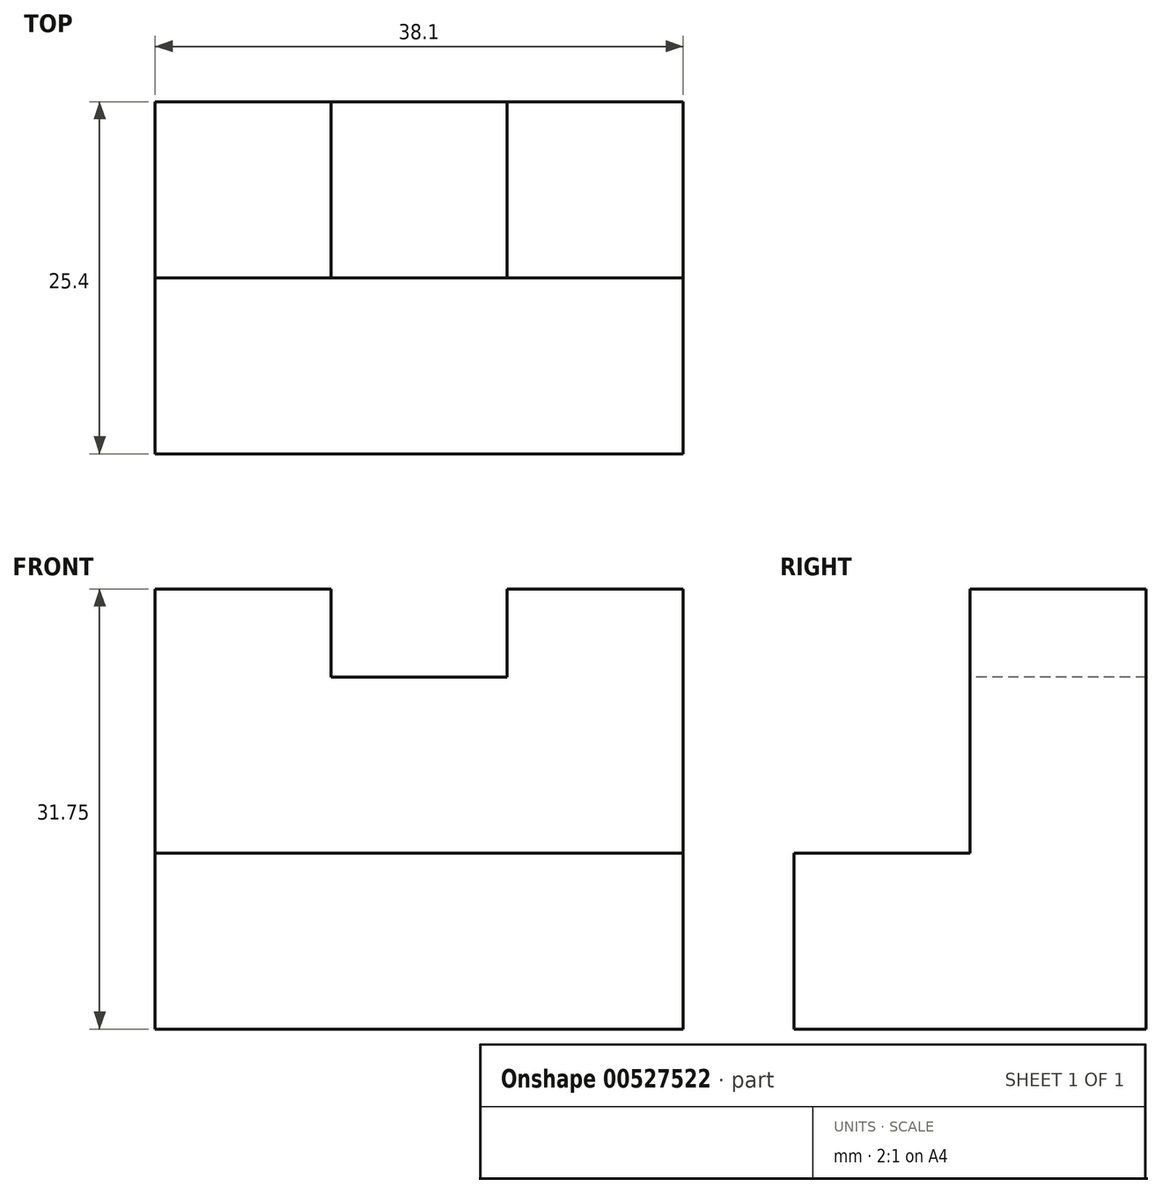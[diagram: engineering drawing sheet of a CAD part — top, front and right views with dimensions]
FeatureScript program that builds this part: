
annotation { "Feature Type Name" : "Feature", "Feature Type Description" : "" }
export const myFeature = defineFeature(function(context is Context, id is Id, definition is map)
    precondition{}
    {
        {
            var Q0;
            Q0=qCreatedBy(makeId("Right.planeOp"),FACE);
            var sketch = newSketch(context, id + "F0", { "sketchPlane" : qUnion([Q0])});
            skLineSegment(sketch, "E0", {"start": v(0, 0) * mm, "end": v(25.4, 0) * mm});
            skLineSegment(sketch, "E1", {"start": v(25.4, 0) * mm, "end": v(25.4, 31.75) * mm});
            skLineSegment(sketch, "E2", {"start": v(25.4, 31.75) * mm, "end": v(12.7, 31.75) * mm});
            skLineSegment(sketch, "E3", {"start": v(12.7, 31.75) * mm, "end": v(12.7, 12.7) * mm});
            skLineSegment(sketch, "E4", {"start": v(12.7, 12.7) * mm, "end": v(0, 12.7) * mm});
            skLineSegment(sketch, "E5", {"start": v(0, 12.7) * mm, "end": v(0, 0) * mm});
            skSolve(sketch);
        }
        {
            var Q0;
            Q0=makeQuery(id+"F0.imprint","IMPRINT",FACE,{"disambiguationData":[TD([[makeQuery(id+"F0.imprint","IMPRINT",EDGE,{"derivedFrom":sQuery(id+"F0.wireOp",EDGE,"E0")}),1.0]])]});
            extrude(context, id + "F1", {"entities" : qUnion([Q0]), "depth" : 38.1 * mm, "offsetDistance" : 25.4 * mm});
        }
        {
            var Q0;
            Q0=makeQuery(id+"F1.opExtrude","SWEPT_FACE",FACE,{"disambiguationData":[OSD([sQuery(id+"F0.wireOp",EDGE,"E2")])]});
            var sketch = newSketch(context, id + "F2", { "sketchPlane" : qUnion([Q0])});
            skLineSegment(sketch, "E6", {"start": v(12.7, 25.4) * mm, "end": v(12.7, 12.7) * mm});
            skLineSegment(sketch, "E7", {"start": v(12.7, 12.7) * mm, "end": v(25.4, 12.7) * mm});
            skLineSegment(sketch, "E8", {"start": v(25.4, 12.7) * mm, "end": v(25.4, 25.4) * mm});
            skLineSegment(sketch, "E9", {"start": v(25.4, 25.4) * mm, "end": v(12.7, 25.4) * mm});
            skSolve(sketch);
        }
        {
            var Q0;
            Q0=makeQuery(id+"F2.imprint","IMPRINT",FACE,{"disambiguationData":[TD([[makeQuery(id+"F2.imprint","IMPRINT",EDGE,{"derivedFrom":sQuery(id+"F2.wireOp",EDGE,"E6")}),1.0]])]});
            extrude(context, id + "F3", {"entities" : qUnion([Q0]), "operationType" : NewBodyOperationType.REMOVE, "oppositeDirection" : true, "depth" : 6.35 * mm, "offsetDistance" : 25.4 * mm});
        }
    });
